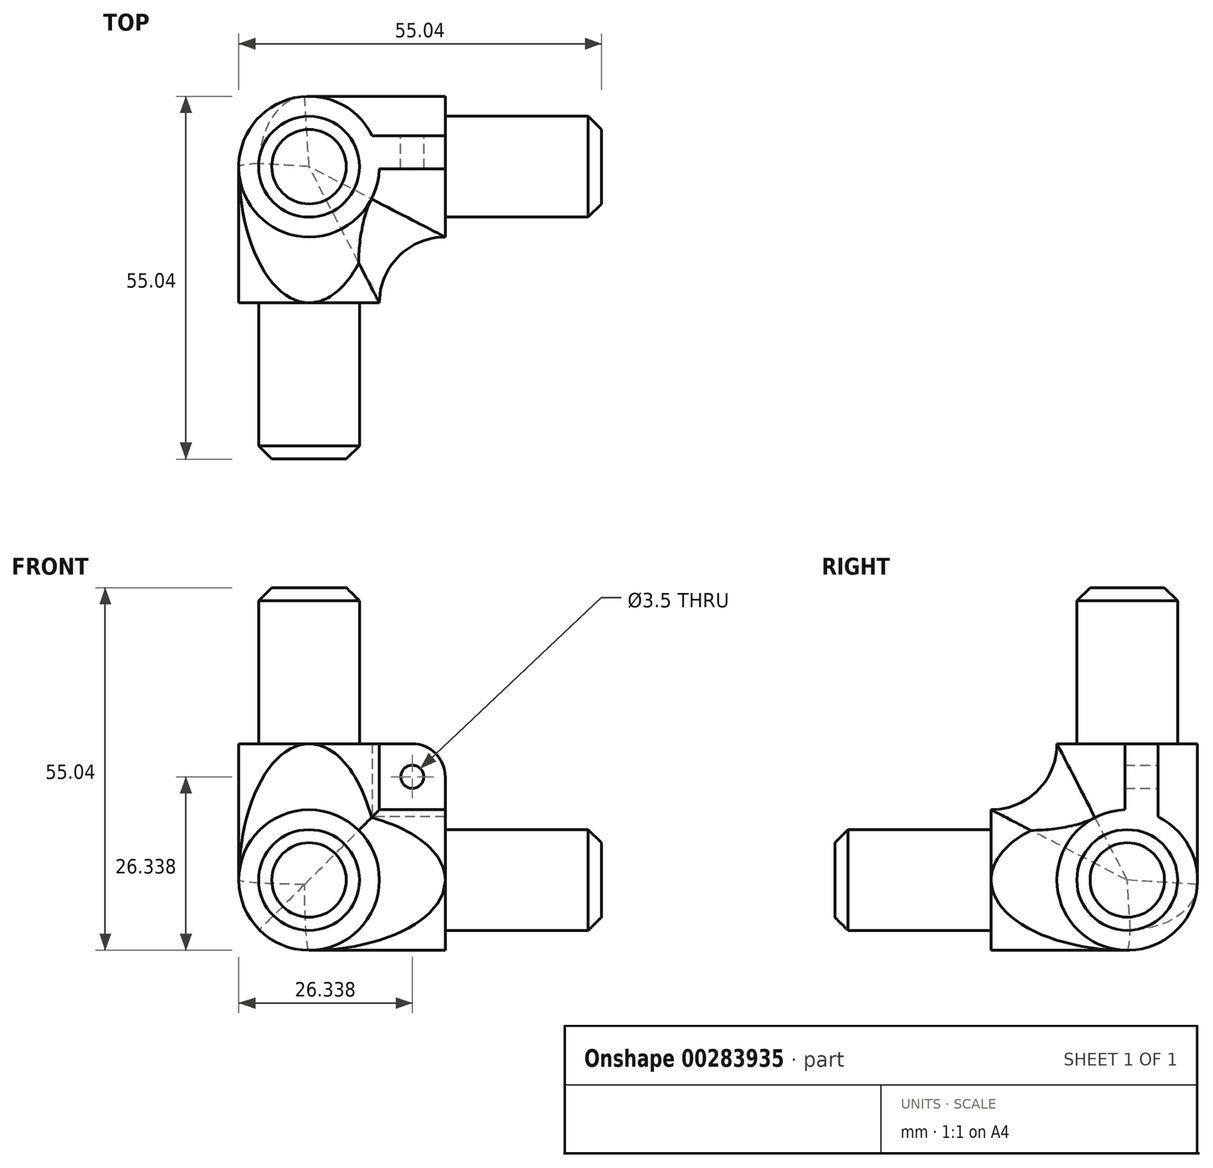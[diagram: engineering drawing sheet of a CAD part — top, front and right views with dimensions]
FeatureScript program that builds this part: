
annotation { "Feature Type Name" : "Feature", "Feature Type Description" : "" }
export const myFeature = defineFeature(function(context is Context, id is Id, definition is map)
    precondition{}
    {
        {
            var Q0;
            Q0=qCreatedBy(makeId("Front.planeOp"),FACE);
            var sketch = newSketch(context, id + "F0", { "sketchPlane" : qUnion([Q0])});
            skCircle(sketch, "E0", {"center": v(0, 0) * mm, "radius": 10.67 * mm});
            skSolve(sketch);
        }
        {
            var Q0;
            Q0=qSketchRegion(id+"F0",true);
            extrude(context, id + "F1", {"entities" : qUnion([Q0]), "depth" : 21.34 * mm / 2 + 10 * mm});
        }
        {
            var Q0;
            Q0=qCreatedBy(makeId("Top.planeOp"),FACE);
            var sketch = newSketch(context, id + "F2", { "sketchPlane" : qUnion([Q0])});
            skCircle(sketch, "E1", {"center": v(0, 0) * mm, "radius": 10.67 * mm});
            skSolve(sketch);
        }
        {
            var Q0;
            Q0=qSketchRegion(id+"F2",true);
            extrude(context, id + "F3", {"entities" : qUnion([Q0]), "operationType" : NewBodyOperationType.ADD, "depth" : 21.34 * mm / 2 + 10 * mm});
        }
        {
            var Q0;
            Q0=qCreatedBy(makeId("Right.planeOp"),FACE);
            var sketch = newSketch(context, id + "F4", { "sketchPlane" : qUnion([Q0])});
            skCircle(sketch, "E2", {"center": v(0, 0) * mm, "radius": 10.67 * mm});
            skSolve(sketch);
        }
        {
            var Q0;
            Q0=qSketchRegion(id+"F4",true);
            extrude(context, id + "F5", {"entities" : qUnion([Q0]), "operationType" : NewBodyOperationType.ADD, "depth" : 21.34 * mm / 2 + 10 * mm});
        }
        {
            var Q0;
            Q0=makeQuery(id+"F1.opExtrude","CAP_FACE",FACE,{"disambiguationData":[OSD([sQuery(id+"F0.wireOp",EDGE,"E0")])],"isStart":true});
            var Q1;
            Q1=makeQuery(id+"F3.opExtrude","SWEPT_FACE",FACE,{"disambiguationData":[OSD([sQuery(id+"F2.wireOp",EDGE,"E1")])]});
            extrude(context, id + "F6", {"entities" : qUnion([Q0]), "operationType" : NewBodyOperationType.ADD, "endBound" : BoundingType.UP_TO_SURFACE, "endBoundEntityFace" : qUnion([Q1]), "depth" : 25 * mm});
        }
        {
            var Q0;
            Q0=makeQuery(id+"F6.opExtrude","SWEPT_FACE",FACE,{"disambiguationData":[OSD([sQuery(id+"F0.wireOp",EDGE,"E0"),sQuery(id+"F4.wireOp",EDGE,"E2")])]});
            extrude(context, id + "F7", {"entities" : qUnion([Q0]), "operationType" : NewBodyOperationType.REMOVE, "endBound" : BoundingType.THROUGH_ALL, "oppositeDirection" : true, "depth" : 25 * mm});
        }
        {
            var Q0;
            Q0=makeQuery(id+"F5.opExtrude","CAP_FACE",FACE,{"disambiguationData":[OSD([sQuery(id+"F4.wireOp",EDGE,"E2")])],"isStart":false});
            var sketch = newSketch(context, id + "F8", { "sketchPlane" : qUnion([Q0])});
            skCircle(sketch, "E3", {"center": v(0, 0) * mm, "radius": 7.65 * mm});
            skSolve(sketch);
        }
        {
            var Q0;
            Q0=qSketchRegion(id+"F8",true);
            extrude(context, id + "F9", {"entities" : qUnion([Q0]), "operationType" : NewBodyOperationType.ADD, "depth" : 1.5 * 15.8 * mm});
        }
        {
            var Q0;
            Q0=makeQuery(id+"F1.opExtrude","CAP_FACE",FACE,{"disambiguationData":[OSD([sQuery(id+"F0.wireOp",EDGE,"E0")])],"isStart":false});
            var sketch = newSketch(context, id + "F10", { "sketchPlane" : qUnion([Q0])});
            skCircle(sketch, "E4", {"center": v(0, 0) * mm, "radius": 7.65 * mm});
            skSolve(sketch);
        }
        {
            var Q0;
            Q0=qSketchRegion(id+"F10",true);
            extrude(context, id + "F11", {"entities" : qUnion([Q0]), "operationType" : NewBodyOperationType.ADD, "depth" : 1.5 * 15.8 * mm});
        }
        {
            var Q0;
            Q0=makeQuery(id+"F3.opExtrude","CAP_FACE",FACE,{"disambiguationData":[OSD([sQuery(id+"F2.wireOp",EDGE,"E1")])],"isStart":false});
            var sketch = newSketch(context, id + "F12", { "sketchPlane" : qUnion([Q0])});
            skCircle(sketch, "E5", {"center": v(0, 0) * mm, "radius": 7.65 * mm});
            skSolve(sketch);
        }
        {
            var Q0;
            Q0=qSketchRegion(id+"F12",true);
            extrude(context, id + "F13", {"entities" : qUnion([Q0]), "operationType" : NewBodyOperationType.ADD, "depth" : 1.5 * 15.8 * mm});
        }
        {
            var Q0;
            Q0=makeQuery(id+"F13.opExtrude","CAP_EDGE",EDGE,{"disambiguationData":[OSD([sQuery(id+"F12.wireOp",EDGE,"E5")])],"isStart":false});
            var Q1;
            Q1=makeQuery(id+"F9.opExtrude","CAP_EDGE",EDGE,{"disambiguationData":[OSD([sQuery(id+"F8.wireOp",EDGE,"E3")])],"isStart":false});
            var Q2;
            Q2=makeQuery(id+"F11.opExtrude","CAP_EDGE",EDGE,{"disambiguationData":[OSD([sQuery(id+"F10.wireOp",EDGE,"E4")])],"isStart":false});
            chamfer(context, id + "F14", {"entities" : qUnion([Q0, Q1, Q2]), "width" : 2 * mm, "tangentPropagation" : true});
        }
        {
            var Q0;
            {var subQ0=sQuery(id+"F0.wireOp",EDGE,"E0");Q0=makeQuery(id+"F7.boolean.opBoolean","INTERSECT",EDGE,{"derivedFrom":[makeQuery(id+"F6.boolean.opBoolean","MERGE",FACE,{"derivedFrom":[makeQuery(id+"F1.opExtrude","SWEPT_FACE",FACE,{"disambiguationData":[OSD([subQ0])]}),makeQuery(id+"F6.opExtrude","SWEPT_FACE",FACE,{"disambiguationData":[OSD([subQ0])]})]}),makeQuery(id+"F7.opExtrude","SWEPT_FACE",FACE,{"disambiguationData":[OSD([sQuery(id+"F4.wireOp",EDGE,"E2")])]})]});}
            fillet(context, id + "F15", {"entities" : qUnion([Q0]), "radius" : 10 * mm, "tangentPropagation" : true, "allowEdgeOverflow" : false});
        }
        {
            var Q0;
            {var subQ0=makeQuery(id+"F3.opExtrude","SWEPT_FACE",FACE,{"disambiguationData":[OSD([sQuery(id+"F2.wireOp",EDGE,"E1")])]});var subQ1=sQuery(id+"F0.wireOp",EDGE,"E0");Q0=makeQuery(id+"F6.boolean.opBoolean","MERGE",EDGE,{"derivedFrom":[makeQuery(id+"F3.boolean.opBoolean","INTERSECT",EDGE,{"derivedFrom":[makeQuery(id+"F1.opExtrude","SWEPT_FACE",FACE,{"disambiguationData":[OSD([subQ1])]}),subQ0]}),makeQuery(id+"F6.opExtrude","TWEAK_EDGE",EDGE,{"derivedFrom":[makeQuery(id+"F1.opExtrude","CAP_EDGE",EDGE,{"disambiguationData":[OSD([subQ1])],"isStart":true}),subQ0]})]});}
            fillet(context, id + "F16", {"entities" : qUnion([Q0]), "radius" : 10 * mm, "tangentPropagation" : true, "allowEdgeOverflow" : false});
        }
        {
            var Q0;
            Q0=makeQuery(id+"F5.opExtrude","CAP_FACE",FACE,{"disambiguationData":[OSD([sQuery(id+"F4.wireOp",EDGE,"E2")])],"isStart":false});
            var sketch = newSketch(context, id + "F17", { "sketchPlane" : qUnion([Q0])});
            skLineSegment(sketch, "E6", {"start": v(0, 0) * mm, "end": v(0, 27.9) * mm, "construction": true});
            skArc(sketch, "E7.0", {"start": v(-10.67, 0) * mm, "mid": v(7.54, -7.54) * mm, "end": v(0, 10.67) * mm, "construction": true});
            skPoint(sketch, "E8", {"position": v(10.67, 0) * mm});
            skLineSegment(sketch, "E9.bottom", {"start": v(4.67, 0) * mm, "end": v(-0.33, 0) * mm});
            skLineSegment(sketch, "E9.top", {"start": v(4.67, 20.67) * mm, "end": v(-0.33, 20.67) * mm});
            skLineSegment(sketch, "E9.left", {"start": v(4.67, 0) * mm, "end": v(4.67, 20.67) * mm});
            skLineSegment(sketch, "E9.right", {"start": v(-0.33, 0) * mm, "end": v(-0.33, 20.67) * mm});
            skLineSegment(sketch, "E10.0", {"start": v(-10.67, 20.67) * mm, "end": v(0, 20.67) * mm, "construction": true});
            skSolve(sketch);
        }
        {
            var Q0;
            Q0 = qSketchRegion(id + "F17", true);
            var Q1;
            Q1=makeQuery(id+"F16.opFillet","BLEND_FACE",FACE,{"disambiguationData":[OSD([sQuery(id+"F2.wireOp",EDGE,"E1"),sQuery(id+"F4.wireOp",EDGE,"E2")]),OD(1.0)]});
            extrude(context, id + "F18", {"entities" : qUnion([Q0]), "operationType" : NewBodyOperationType.ADD, "oppositeDirection" : true, "endBoundEntityFace" : qUnion([Q1]), "depth" : 20 * mm});
        }
        {
            var Q0;
            Q0=makeQuery(id+"F18.opExtrude","CAP_EDGE",EDGE,{"disambiguationData":[OSD([sQuery(id+"F17.wireOp",EDGE,"E9.top")])],"isStart":true});
            var Q1;
            Q1=makeQuery(id+"F18.boolean.opBoolean","INTERSECT",EDGE,{"derivedFrom":[makeQuery(id+"F16.opFillet","BLEND_FACE",FACE,{"disambiguationData":[OSD([sQuery(id+"F2.wireOp",EDGE,"E1"),sQuery(id+"F4.wireOp",EDGE,"E2")]),OD(1.0)]}),makeQuery(id+"F18.opExtrude","SWEPT_FACE",FACE,{"disambiguationData":[OSD([sQuery(id+"F17.wireOp",EDGE,"E9.right")])]})]});
            fillet(context, id + "F19", {"entities" : qUnion([Q0, Q1]), "radius" : 5 * mm, "tangentPropagation" : true, "allowEdgeOverflow" : false});
        }
        {
            var Q0;
            Q0=makeQuery(id+"F18.opExtrude","SWEPT_FACE",FACE,{"disambiguationData":[OSD([sQuery(id+"F17.wireOp",EDGE,"E9.left")])]});
            var sketch = newSketch(context, id + "F20", { "sketchPlane" : qUnion([Q0])});
            skCircle(sketch, "E11", {"center": v(-15.67, 15.67) * mm, "radius": 1.75 * mm});
            skSolve(sketch);
        }
        {
            var Q0;
            Q0 = qSketchRegion(id + "F20", true);
            extrude(context, id + "F21", {"entities" : qUnion([Q0]), "operationType" : NewBodyOperationType.REMOVE, "endBound" : BoundingType.THROUGH_ALL, "oppositeDirection" : true, "depth" : 25 * mm});
        }
    });
